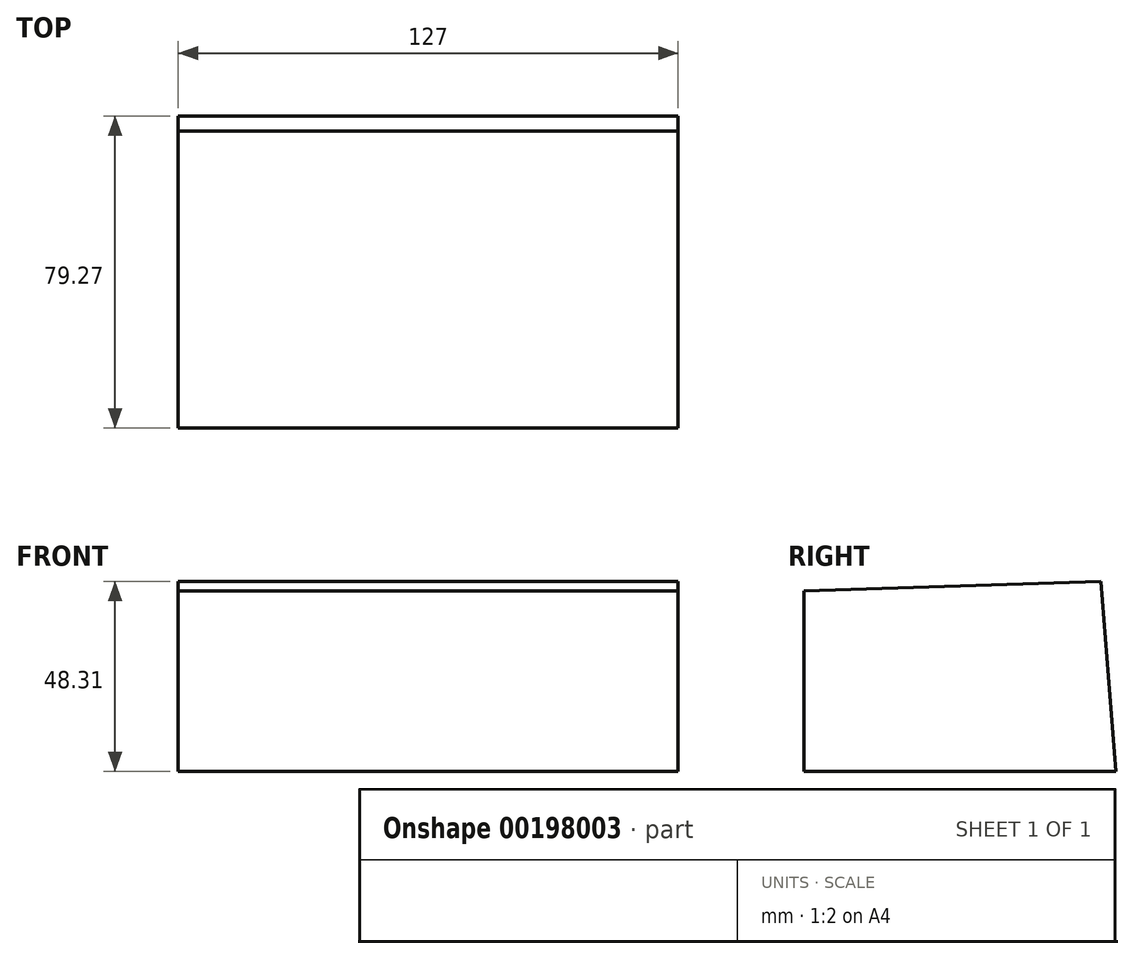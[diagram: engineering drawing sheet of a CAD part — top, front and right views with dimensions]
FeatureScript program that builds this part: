
annotation { "Feature Type Name" : "Feature", "Feature Type Description" : "" }
export const myFeature = defineFeature(function(context is Context, id is Id, definition is map)
    precondition{}
    {
        {
            var Q0;
            Q0=qCreatedBy(makeId("Right.planeOp"),FACE);
            var sketch = newSketch(context, id + "F0", { "sketchPlane" : qUnion([Q0])});
            skLineSegment(sketch, "E0", {"start": v(0, 0) * mm, "end": v(-44.57, 0) * mm});
            skLineSegment(sketch, "E1", {"start": v(-44.57, 0) * mm, "end": v(-44.57, 45.91) * mm});
            skLineSegment(sketch, "E2", {"start": v(-44.57, 45.91) * mm, "end": v(30.8, 48.3) * mm});
            skLineSegment(sketch, "E3", {"start": v(30.8, 48.3) * mm, "end": v(34.7, 0) * mm});
            skLineSegment(sketch, "E4", {"start": v(34.7, 0) * mm, "end": v(0, 0) * mm});
            skSolve(sketch);
        }
        {
            var Q0;
            Q0 = qSketchRegion(id + "F0", true);
            extrude(context, id + "F1", {"entities" : qUnion([Q0]), "depth" : 127 * mm});
        }
    });
